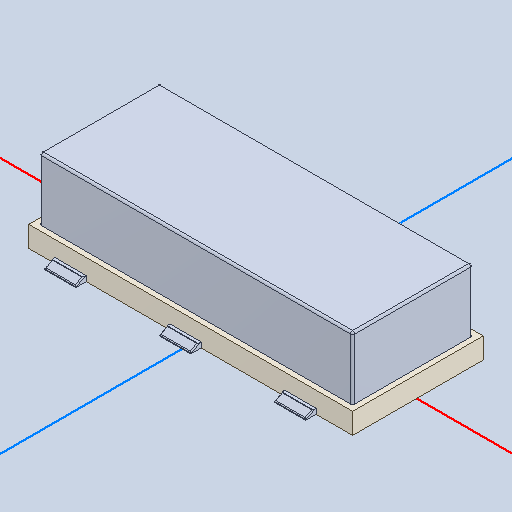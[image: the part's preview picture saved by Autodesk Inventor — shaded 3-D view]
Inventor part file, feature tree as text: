
AUTODESK INVENTOR PART (.ipt)
format: ipt  version: 2022 (Build 260153000, 153)  size: 159,232 bytes
history: native  units: mm
features: other x11, mirror x3, fillet x2
ambient origin geometry x8: Origin, YZ Plane, XZ Plane, XY Plane, X Axis, Y Axis, Z Axis, Center Point
bodies: Body1 (feature_tree), Body2 (feature_tree), Body3 (feature_tree), Body4 (feature_tree), Body5 (feature_tree), Body6 (feature_tree), Body7 (feature_tree), Body8 (feature_tree)
feature tree (16):
  other  "Твердое тело1"
  other  "Твердое тело2"
  other  "Твердое тело3"
  other  "Твердое тело4"
  other  "Твердое тело5"
  other  "Твердое тело6"
  other  "Твердое тело7"
  other  "Твердое тело8"
  fillet  "Fillet2"  [1 undecoded]
  other  "Boss-Extrude2"
  fillet  "Fillet1"  [1 undecoded]
  other  "LPattern1[1]"
  other  "LPattern1[2]"
  mirror  "Mirror1[1]"
  mirror  "Mirror1[2]"
  mirror  "Mirror1[3]"
note: 2 required parameter values undecoded (feature->parameter linkage not recoverable at this tier; creation-order binding heuristic only, values carry confidence <= 0.55)
